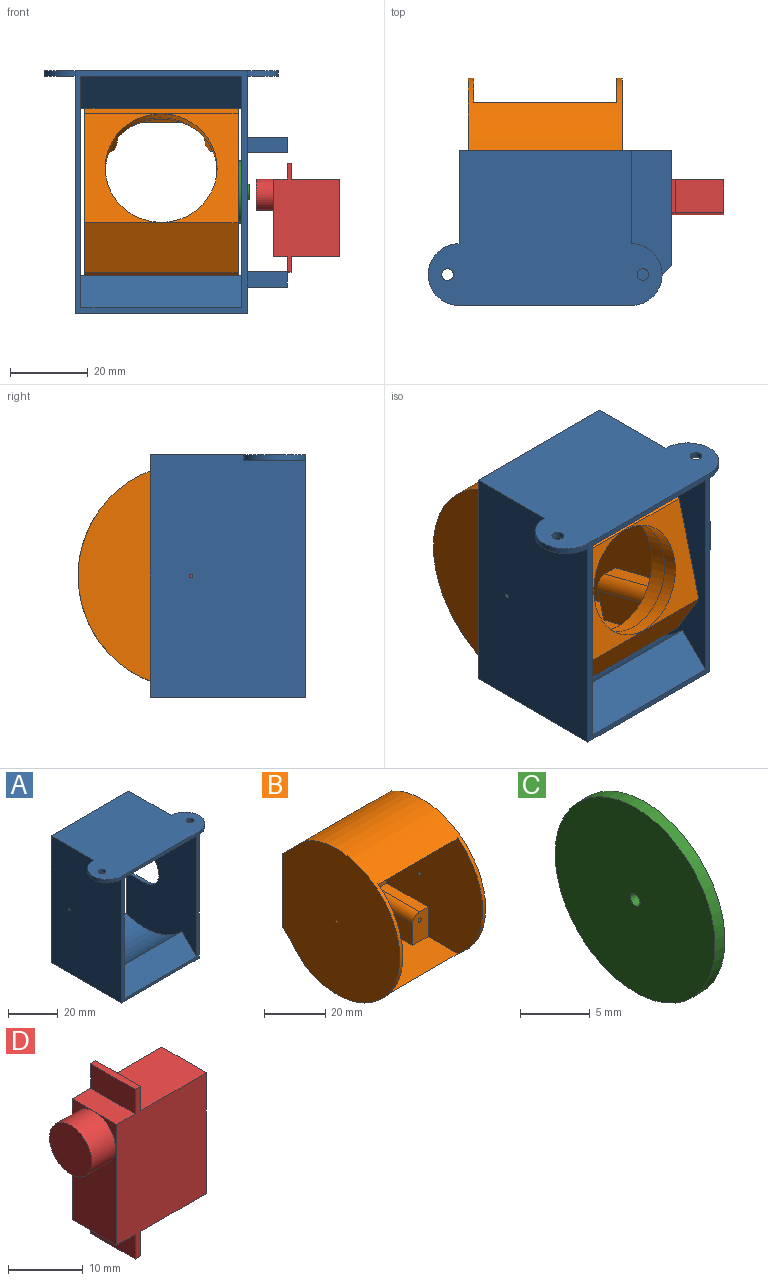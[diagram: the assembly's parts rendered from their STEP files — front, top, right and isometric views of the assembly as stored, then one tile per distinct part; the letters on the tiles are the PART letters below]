
ASSEMBLY  parts=4 mates=4
PART A: 36 faces, bbox 62.4x39.9x62.4 mm
  f0: plane 62.4x54.5mm, normal (0,1,0), area 477.2mm2, adj f1,f3,f4,f5,f6,f7,f8,f9
  f1: plane 60.4x39.94mm, normal (1,0,0), area 2108.5mm2, adj f0,f11,f16,f17,f18,f19,f30,f31
  f2: cylinder r=0.5mm len=1mm, axis (1,0,0), area 3.1mm2, adj f15,f33
  f3: plane 29.64x4mm, normal (1,0,0), area 118.5mm2, adj f0,f4,f5,f29
  f4: plane 39.94x10.3mm, normal (0,0,1), area 358.3mm2, adj f0,f3,f10,f29
  f5: plane 39.94x10.3mm, normal (0,0,-1), area 358.3mm2, adj f0,f3,f9,f29
  f6: plane 29.64x4mm, normal (1,0,0), area 118.5mm2, adj f0,f7,f8,f28
  f7: plane 39.94x10.3mm, normal (0,0,1), area 358.3mm2, adj f0,f6,f9,f28
  f8: plane 39.94x10.3mm, normal (0,0,-1), area 358.3mm2, adj f0,f6,f14,f28
  f9: plane 39.94x30.48mm, normal (1,0,0), area 945.1mm2, adj f0,f5,f7,f11,f21,f22,f23
  f10: plane 39.94x17.17mm, normal (1,0,0), area 661.7mm2, adj f0,f4,f11,f12,f25,f35
  f11: plane 62.4x44.2mm, normal (0,-1,0), area 303.2mm2, adj f1,f9,f10,f12,f13,f14,f15,f17
  f12: plane 60.1x39.94mm, normal (0,0,1), area 1949.6mm2, adj f0,f10,f11,f15,f24,f26,f34,f35
  f13: plane 44.2x39.94mm, normal (0,0,-1), area 1765.1mm2, adj f0,f11,f14,f15
  f14: plane 39.94x6.75mm, normal (1,0,0), area 269.7mm2, adj f0,f8,f11,f13
  f15: plane 62.4x39.94mm, normal (-1,0,0), area 2467.3mm2, adj f0,f2,f11,f12,f13,f27,f34
  f16: cylinder r=30.2mm len=41.2mm, axis (1,0,0), area 1407.7mm2, adj f0,f1,f17,f20
  f17: plane 41.2x8.29mm, normal (0,-0.71,-0.71), area 483.1mm2, adj f1,f11,f16,f20
  f18: plane 41.2x8.29mm, normal (0,-0.71,0.71), area 483.1mm2, adj f1,f11,f19,f20
  f19: cylinder r=30.2mm len=41.2mm, axis (1,0,0), area 1407.7mm2, adj f0,f1,f18,f20
  f20: plane 60.4x39.94mm, normal (-1,0,0), area 1936.8mm2, adj f0,f11,f16,f17,f18,f19,f21,f22
  f21: plane 10.44x1.5mm, normal (0,0,-1), area 15.7mm2, adj f0,f9,f20,f22
  f22: cylinder r=8.1mm len=16.2mm, axis (1,0,0), area 38.2mm2, adj f9,f20,f21,f23
  f23: plane 10.44x1.5mm, normal (0,0,1), area 15.7mm2, adj f0,f9,f20,f22
  f24: cylinder r=1.5mm len=3mm, axis (0,0,1), area 14.1mm2, adj f12,f25
  f25: plane 15.9x7.95mm, normal (0,0,-1), area 92.2mm2, adj f10,f24,f35
  f26: cylinder r=1.5mm len=3mm, axis (0,0,1), area 14.1mm2, adj f12,f27
  f27: plane 15.9x7.95mm, normal (0,0,-1), area 92.2mm2, adj f15,f26,f34
  f28: plane 10.3x10.3mm, normal (0.71,-0.71,0), area 58.3mm2, adj f6,f7,f8,f11
  f29: plane 10.3x10.3mm, normal (0.71,-0.71,0), area 58.3mm2, adj f3,f4,f5,f11
  f30: plane 10.44x0.5mm, normal (0,0,-1), area 5.2mm2, adj f0,f1,f31,f33
  f31: cylinder r=3.75mm len=7.5mm, axis (1,0,0), area 5.9mm2, adj f1,f30,f32,f33
  f32: plane 10.44x0.5mm, normal (0,0,1), area 5.2mm2, adj f0,f1,f31,f33
  f33: plane 14.19x7.5mm, normal (1,0,0), area 99.6mm2, adj f0,f2,f30,f31,f32
  f34: cylinder r=7.95mm len=15.9mm, axis (0,0,1), area 37.5mm2, adj f11,f12,f15,f27
  f35: cylinder r=7.95mm len=15.9mm, axis (0,0,1), area 37.5mm2, adj f10,f11,f12,f25
PART B: 40 faces, bbox 39.5x54.1x58 mm
  f0: plane 11.75x7.13mm, normal (0,-1,0), area 79.7mm2, adj f10,f13,f18,f19,f20,f33
  f1: plane 11.75x7.13mm, normal (0,-1,0), area 79.7mm2, adj f10,f11,f15,f16,f17,f31
  f2: plane 11.75x7.13mm, normal (0,-1,0), area 79.7mm2, adj f12,f13,f21,f22,f23,f27
  f3: plane 11.75x7.13mm, normal (0,-1,0), area 79.7mm2, adj f11,f12,f24,f25,f26,f29
  f4: plane 39.5x29mm, normal (0,1,0), area 496.3mm2, adj f5,f7,f8,f9,f39
  f5: plane 39.5x10.61mm, normal (0,0.71,0.71), area 593mm2, adj f4,f6,f8,f9
  f6: cylinder r=29mm len=58mm, axis (-1,0,0), area 2846mm2, adj f5,f7,f8,f9,f10,f11,f12,f13
  f7: plane 39.5x10.61mm, normal (0,0.71,-0.71), area 593mm2, adj f4,f6,f8,f9
  f8: plane 58x54.11mm, normal (1,0,0), area 2545.3mm2, adj f4,f5,f6,f7,f38
  f9: plane 58x54.11mm, normal (-1,0,0), area 2545.3mm2, adj f4,f5,f6,f7,f37
  f10: plane 46x44.11mm, normal (-1,0,0), area 1424.5mm2, adj f0,f1,f6,f11,f13,f14,f17,f18
  f11: plane 36.75x32.78mm, normal (0,0,1), area 933.9mm2, adj f1,f3,f6,f10,f12,f14,f15,f26
  f12: plane 46x44.11mm, normal (1,0,0), area 1424.5mm2, adj f2,f3,f6,f11,f13,f14,f23,f24
  f13: plane 36.75x32.78mm, normal (0,0,-1), area 933.9mm2, adj f0,f2,f6,f10,f12,f14,f20,f21
  f14: plane 46x36.75mm, normal (0,-1,0), area 609.9mm2, adj f10,f11,f12,f13,f15,f16,f17,f18
  f15: plane 19x8.5mm, normal (-1,0,0), area 161.5mm2, adj f1,f11,f14,f16
  f16: cylinder r=3.25mm len=19mm, axis (0,-1,0), area 97mm2, adj f1,f14,f15,f17
  f17: plane 19x3.88mm, normal (0,0,1), area 73.6mm2, adj f1,f10,f14,f16
  f18: plane 19x3.88mm, normal (0,0,-1), area 73.6mm2, adj f0,f10,f14,f19
  f19: cylinder r=3.25mm len=19mm, axis (0,-1,0), area 97mm2, adj f0,f14,f18,f20
  f20: plane 19x8.5mm, normal (-1,0,0), area 161.5mm2, adj f0,f13,f14,f19
  f21: plane 19x8.5mm, normal (1,0,0), area 161.5mm2, adj f2,f13,f14,f22
  f22: cylinder r=3.25mm len=19mm, axis (0,-1,0), area 97mm2, adj f2,f14,f21,f23
  f23: plane 19x3.88mm, normal (0,0,-1), area 73.6mm2, adj f2,f12,f14,f22
  f24: plane 19x3.88mm, normal (0,0,1), area 73.6mm2, adj f3,f12,f14,f25
  f25: cylinder r=3.25mm len=19mm, axis (0,-1,0), area 97mm2, adj f3,f14,f24,f26
  f26: plane 19x8.5mm, normal (1,0,0), area 161.5mm2, adj f3,f11,f14,f25
  f27: cylinder r=0.75mm len=19mm, axis (0,-1,0), area 89.5mm2, adj f2,f28
  f28: plane 1.5x1.5mm, normal (0,-1,0), area 1.8mm2, adj f27
  f29: cylinder r=0.75mm len=19mm, axis (0,-1,0), area 89.5mm2, adj f3,f30
  f30: plane 1.5x1.5mm, normal (0,-1,0), area 1.8mm2, adj f29
  f31: cylinder r=0.75mm len=19mm, axis (0,-1,0), area 89.5mm2, adj f1,f32
  f32: plane 1.5x1.5mm, normal (0,-1,0), area 1.8mm2, adj f31
  f33: cylinder r=0.75mm len=19mm, axis (0,-1,0), area 89.5mm2, adj f0,f34
  f34: plane 1.5x1.5mm, normal (0,-1,0), area 1.8mm2, adj f33
  f35: plane 31x31mm, normal (0,-1,0), area 105.6mm2, adj f36,f39
  f36: cylinder r=15.5mm len=31mm, axis (0,-1,0), area 584.3mm2, adj f14,f35
  f37: cylinder r=0.5mm len=1.38mm, axis (1,0,0), area 4.3mm2, adj f9,f12
  f38: cylinder r=0.5mm len=1.38mm, axis (1,0,0), area 4.3mm2, adj f8,f10
  f39: cylinder r=14.38mm len=28.75mm, axis (0,-1,0), area 361.3mm2, adj f4,f35
PART C: 8 faces, bbox 3x16.2x16.2 mm
  f0: plane 2.8x2.8mm, normal (1,0,0), area 5.4mm2, adj f1,f5
  f1: cylinder r=0.5mm len=1mm, axis (-1,0,0), area 3.1mm2, adj f0,f4
  f2: cylinder r=8.1mm len=16.2mm, axis (-1,0,0), area 50.9mm2, adj f3,f4
  f3: plane 16.2x16.2mm, normal (1,0,0), area 193.6mm2, adj f2,f6
  f4: plane 16.2x16.2mm, normal (-1,0,0), area 205.3mm2, adj f1,f2
  f5: cylinder r=1.4mm len=2.8mm, axis (-1,0,0), area 17.6mm2, adj f0,f7
  f6: cylinder r=2mm len=4mm, axis (-1,0,0), area 25.1mm2, adj f3,f7
  f7: plane 4x4mm, normal (1,0,0), area 6.4mm2, adj f5,f6
PART D: 16 faces, bbox 21.5x8.5x27.8 mm
  f0: plane 8.46x3.5mm, normal (0,0,1), area 29.6mm2, adj f2,f4,f7,f15
  f1: plane 8.46x3.5mm, normal (0,0,-1), area 29.6mm2, adj f2,f4,f7,f12
  f2: plane 27.8x17mm, normal (0,-1,0), area 344.6mm2, adj f0,f1,f3,f5,f6,f7,f10,f11
  f3: plane 12.5x8.46mm, normal (0,0,-1), area 105.7mm2, adj f2,f4,f6,f11
  f4: plane 27.8x17mm, normal (0,1,0), area 344.6mm2, adj f0,f1,f3,f5,f6,f7,f10,f11
  f5: plane 12.5x8.46mm, normal (0,0,1), area 105.8mm2, adj f2,f4,f6,f14
  f6: plane 19.8x8.46mm, normal (1,0,0), area 167.5mm2, adj f2,f3,f4,f5
  f7: plane 19.8x8.46mm, normal (-1,0,0), area 117.2mm2, adj f0,f1,f2,f4,f8
  f8: cylinder r=4mm len=8mm, axis (1,0,0), area 113.1mm2, adj f7,f9
  f9: plane 8x8mm, normal (-1,0,0), area 50.3mm2, adj f8
  f10: plane 8.46x1mm, normal (0,0,-1), area 8.5mm2, adj f2,f4,f11,f12
  f11: plane 8.46x4mm, normal (1,0,0), area 33.8mm2, adj f2,f3,f4,f10
  f12: plane 8.46x4mm, normal (-1,0,0), area 33.8mm2, adj f1,f2,f4,f10
  f13: plane 8.46x1mm, normal (0,0,1), area 8.5mm2, adj f2,f4,f14,f15
  f14: plane 8.46x4mm, normal (1,0,0), area 33.8mm2, adj f2,f4,f5,f13
  f15: plane 8.46x4mm, normal (-1,0,0), area 33.8mm2, adj f0,f2,f4,f13
PLACE A t=(34.67,-65.18,38.96)mm
PLACE B rot(axis=(1,0,0),165.8deg) t=(35.02,-65.18,38.96)mm
PLACE C rot(axis=(-1,0,0),14.2deg) t=(35.02,-65.18,38.96)mm
PLACE D rot(axis=(-1,0,0),1.3deg) t=(36.17,-66.64,38.2)mm
MATE planar C.f1 <-> B.f8  axis (-1,0,0) through (54.77,-65.18,38.96)mm
MATE planar A.f6 <-> D.f12  axis (1,0,0) through (67.42,-69.56,16.51)mm
MATE revolute B.f6 <-> A.f2  axis (-1,0,0) through (35.02,-65.18,38.96)mm
MATE slider C.f1 <-> B.f6  axis (-1,0,0) through (55.77,-65.18,38.96)mm
